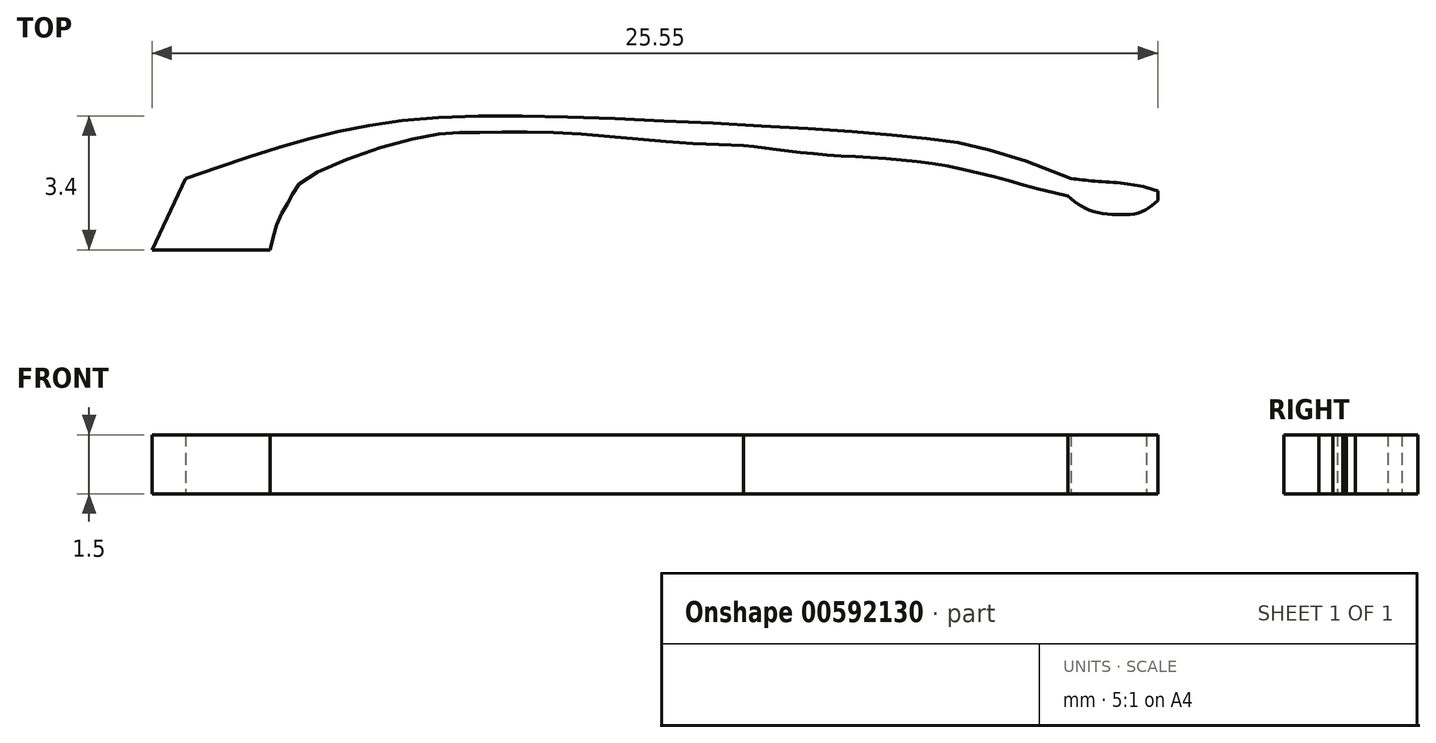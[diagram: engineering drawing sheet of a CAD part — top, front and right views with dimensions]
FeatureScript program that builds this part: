
annotation { "Feature Type Name" : "Feature", "Feature Type Description" : "" }
export const myFeature = defineFeature(function(context is Context, id is Id, definition is map)
    precondition{}
    {
        {
            var Q0;
            Q0=qCreatedBy(makeId("Top.planeOp"),FACE);
            var sketch = newSketch(context, id + "F0", { "sketchPlane" : qUnion([Q0])});
            skLineSegment(sketch, "E0", {"start": v(-33.88, -7.6) * mm, "end": v(-32.18, -3.97) * mm});
            skFitSpline(sketch, "E1", {"points": [v(-32.18, -3.97) * mm, v(-26.13, -2) * mm, v(-19.7, -0.9) * mm, v(-7.38, -1.07) * mm, v(4.7, -1.85) * mm, v(12.82, -3.97) * mm], "startDerivative": vector(38.63, 13.41) * mm, "endDerivative": vector(60.05, -24.37) * mm});
            skLineSegment(sketch, "E2", {"start": v(-33.88, -7.6) * mm, "end": v(-27.88, -7.6) * mm});
            skFitSpline(sketch, "E3", {"points": [v(-27.88, -7.6) * mm, v(-27.63, -6.6) * mm, v(-27.23, -5.63) * mm, v(-26.83, -4.93) * mm, v(-26.27, -4.14) * mm, v(-20.43, -1.9) * mm, v(-17.27, -1.64) * mm, v(-13.34, -1.64) * mm, v(-8.2, -2.07) * mm, v(-3.82, -2.3) * mm], "startDerivative": vector(3.1, 14.24) * mm, "endDerivative": vector(27.9, -1.3) * mm});
            skFitSpline(sketch, "E4", {"points": [v(-3.82, -2.3) * mm, v(0, -2.74) * mm, v(6.23, -3.3) * mm, v(12.66, -4.88) * mm], "startDerivative": vector(12.18, -0.98) * mm, "endDerivative": vector(17.4, -3.94) * mm});
            skFitSpline(sketch, "E5", {"points": [v(12.82, -3.97) * mm, v(13.82, -4.1) * mm, v(15.39, -4.2) * mm, v(16.64, -4.42) * mm], "startDerivative": vector(3.16, -0.45) * mm, "endDerivative": vector(3.59, -0.74) * mm});
            skFitSpline(sketch, "E6", {"points": [v(12.66, -4.88) * mm, v(13.64, -5.54) * mm, v(15.13, -5.8) * mm, v(16.36, -5.68) * mm, v(17.22, -5.1) * mm], "startDerivative": vector(3.64, -3.1) * mm, "endDerivative": vector(3.5, 2.97) * mm});
            skLineSegment(sketch, "E7", {"start": v(17.22, -5.1) * mm, "end": v(17.22, -4.6) * mm});
            skFitSpline(sketch, "E8", {"points": [v(16.64, -4.42) * mm, v(17.22, -4.6) * mm], "startDerivative": vector(0.58, -0.18) * mm, "endDerivative": vector(0.58, -0.18) * mm});
            skSolve(sketch);
        }
        {
            var Q0;
            Q0 = qSketchRegion(id + "F0", true);
            extrude(context, id + "F1", {"entities" : qUnion([Q0]), "depth" : 3 * mm, "offsetDistance" : 25 * mm});
        }
        {
            var Q0;
            Q0=makeQuery(id+"F1.opExtrude","SWEPT_BODY",BODY,{"disambiguationData":[OSD([sQuery(id+"F0.wireOp",EDGE,"E0"),sQuery(id+"F0.wireOp",EDGE,"E1"),sQuery(id+"F0.wireOp",EDGE,"E2"),sQuery(id+"F0.wireOp",EDGE,"E3"),sQuery(id+"F0.wireOp",EDGE,"E4"),sQuery(id+"F0.wireOp",EDGE,"E5"),sQuery(id+"F0.wireOp",EDGE,"E6"),sQuery(id+"F0.wireOp",EDGE,"E7"),sQuery(id+"F0.wireOp",EDGE,"E8")])]});
            var Q1;
            Q1=qCreatedBy(makeId("Origin.pointOp"),VERTEX);
            transform(context, id + "F2", {"entities" : qUnion([Q0]), "transformType" : TransformType.SCALE_UNIFORMLY, "scale" : .5, "scalePoint" : qUnion([Q1]), "makeCopy" : false});
        }
    });
